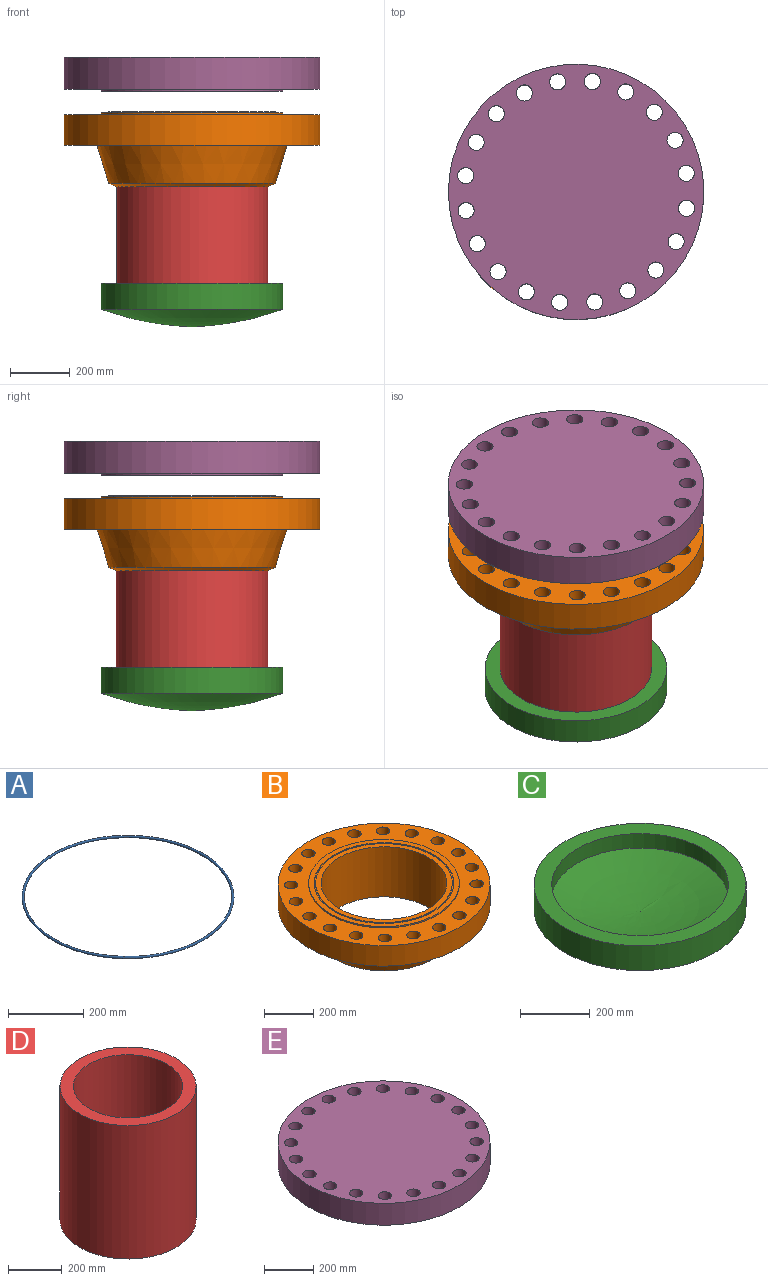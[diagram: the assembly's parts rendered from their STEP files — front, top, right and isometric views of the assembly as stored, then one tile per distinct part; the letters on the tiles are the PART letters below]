
ASSEMBLY  parts=5 mates=4
PART A: 1 faces, bbox 611.7x611.7x6.4 mm
  f0: torus R=279.4mm, axis (0,0,-1), area 35021.1mm2
PART B: 32 faces, bbox 857.3x857.3x247.7 mm
  f0: cylinder r=282.58mm len=565.15mm, axis (0,0,-1), area 7892mm2, adj f1,f11
  f1: plane 565.15x565.15mm, normal (0,0,1), area 11147.6mm2, adj f0,f2
  f2: cylinder r=276.23mm len=552.45mm, axis (0,0,-1), area 7714.6mm2, adj f1,f3
  f3: plane 552.45x552.45mm, normal (0,0,1), area 37021.3mm2, adj f2,f4
  f4: cylinder r=254mm len=508mm, axis (0,0,-1), area 395231.8mm2, adj f3,f5
  f5: cone r=254mm half-angle=67deg, axis (0,0,1), area 46560.4mm2, adj f4,f6
  f6: cone r=319.09mm half-angle=17deg, axis (0,0,1), area 253505.2mm2, adj f5,f7
  f7: plane 857.25x857.25mm, normal (0,0,-1), area 211322.6mm2, adj f6,f8,f12,f13,f14,f15,f16,f17
  f8: cylinder r=428.62mm len=857.25mm, axis (0,0,-1), area 273622mm2, adj f7,f9
  f9: plane 857.25x857.25mm, normal (0,0,1), area 239330.4mm2, adj f8,f10,f12,f13,f14,f15,f16,f17
  f10: cylinder r=304.8mm len=609.6mm, axis (0,0,-1), area 12161mm2, adj f9,f11
  f11: plane 609.6x609.6mm, normal (0,0,1), area 41011.6mm2, adj f0,f10
  f12: cylinder r=27.05mm len=101.6mm, axis (0,0,-1), area 17268.6mm2, adj f7,f9
  f13: cylinder r=27.05mm len=101.6mm, axis (0,0,-1), area 17268.6mm2, adj f7,f9
  f14: cylinder r=27.05mm len=101.6mm, axis (0,0,-1), area 17268.6mm2, adj f7,f9
  f15: cylinder r=27.05mm len=101.6mm, axis (0,0,-1), area 17268.6mm2, adj f7,f9
  f16: cylinder r=27.05mm len=101.6mm, axis (0,0,-1), area 17268.6mm2, adj f7,f9
  f17: cylinder r=27.05mm len=101.6mm, axis (0,0,-1), area 17268.6mm2, adj f7,f9
  f18: cylinder r=27.05mm len=101.6mm, axis (0,0,-1), area 17268.6mm2, adj f7,f9
  f19: cylinder r=27.05mm len=101.6mm, axis (0,0,-1), area 17268.6mm2, adj f7,f9
  f20: cylinder r=27.05mm len=101.6mm, axis (0,0,-1), area 17268.6mm2, adj f7,f9
  f21: cylinder r=27.05mm len=101.6mm, axis (0,0,-1), area 17268.6mm2, adj f7,f9
  f22: cylinder r=27.05mm len=101.6mm, axis (0,0,-1), area 17268.6mm2, adj f7,f9
  f23: cylinder r=27.05mm len=101.6mm, axis (0,0,-1), area 17268.6mm2, adj f7,f9
  f24: cylinder r=27.05mm len=101.6mm, axis (0,0,-1), area 17268.6mm2, adj f7,f9
  f25: cylinder r=27.05mm len=101.6mm, axis (0,0,-1), area 17268.6mm2, adj f7,f9
  f26: cylinder r=27.05mm len=101.6mm, axis (0,0,-1), area 17268.6mm2, adj f7,f9
  f27: cylinder r=27.05mm len=101.6mm, axis (0,0,-1), area 17268.6mm2, adj f7,f9
  f28: cylinder r=27.05mm len=101.6mm, axis (0,0,-1), area 17268.6mm2, adj f7,f9
  f29: cylinder r=27.05mm len=101.6mm, axis (0,0,-1), area 17268.6mm2, adj f7,f9
  f30: cylinder r=27.05mm len=101.6mm, axis (0,0,-1), area 17268.6mm2, adj f7,f9
  f31: cylinder r=27.05mm len=101.6mm, axis (0,0,-1), area 17268.6mm2, adj f7,f9
PART C: 5 faces, bbox 609.9x609.9x145.3 mm
  f0: revolved ~609.92x609.92mm, area 301686.6mm2, adj f1
  f1: cylinder r=304.96mm len=609.92mm, axis (0,0,1), area 166982mm2, adj f0,f2
  f2: plane 609.92x609.92mm, normal (0,0,1), area 89231mm2, adj f1,f3
  f3: cylinder r=254.16mm len=508.32mm, axis (0,0,1), area 81123.6mm2, adj f2,f4
  f4: revolved ~508.32x508.32mm, area 208213.8mm2, adj f3
PART D: 4 faces, bbox 508x508x609.6 mm
  f0: cylinder r=203.99mm len=609.6mm, axis (0,0,-1), area 781318.6mm2, adj f2,f3
  f1: cylinder r=254mm len=609.6mm, axis (0,0,-1), area 972878.4mm2, adj f2,f3
  f2: plane 508x508mm, normal (0,0,1), area 71958.6mm2, adj f0,f1
  f3: plane 508x508mm, normal (0,0,-1), area 71958.6mm2, adj f0,f1
PART E: 27 faces, bbox 857.3x857.3x115.3 mm
  f0: plane 609.6x609.6mm, normal (0,0,-1), area 41482mm2, adj f1,f6
  f1: cylinder r=304.8mm len=609.6mm, axis (0,0,-1), area 11698.7mm2, adj f0,f2
  f2: plane 857.25x857.25mm, normal (0,0,-1), area 239330.4mm2, adj f1,f3,f7,f8,f9,f10,f11,f12
  f3: cylinder r=428.62mm len=857.25mm, axis (0,0,-1), area 290723.4mm2, adj f2,f4
  f4: plane 857.25x857.25mm, normal (0,0,1), area 531193.9mm2, adj f3,f7,f8,f9,f10,f11,f12,f13
  f5: plane 552.98x552.98mm, normal (0,0,-1), area 240164.6mm2, adj f6
  f6: torus R=279.4mm, axis (0,0,-1), area 12923.1mm2, adj f0,f5
  f7: cylinder r=27.05mm len=107.95mm, axis (0,0,-1), area 18347.9mm2, adj f2,f4
  f8: cylinder r=27.05mm len=107.95mm, axis (0,0,-1), area 18347.9mm2, adj f2,f4
  f9: cylinder r=27.05mm len=107.95mm, axis (0,0,-1), area 18347.9mm2, adj f2,f4
  f10: cylinder r=27.05mm len=107.95mm, axis (0,0,-1), area 18347.9mm2, adj f2,f4
  f11: cylinder r=27.05mm len=107.95mm, axis (0,0,-1), area 18347.9mm2, adj f2,f4
  f12: cylinder r=27.05mm len=107.95mm, axis (0,0,-1), area 18347.9mm2, adj f2,f4
  f13: cylinder r=27.05mm len=107.95mm, axis (0,0,-1), area 18347.9mm2, adj f2,f4
  f14: cylinder r=27.05mm len=107.95mm, axis (0,0,-1), area 18347.9mm2, adj f2,f4
  f15: cylinder r=27.05mm len=107.95mm, axis (0,0,-1), area 18347.9mm2, adj f2,f4
  f16: cylinder r=27.05mm len=107.95mm, axis (0,0,-1), area 18347.9mm2, adj f2,f4
  f17: cylinder r=27.05mm len=107.95mm, axis (0,0,-1), area 18347.9mm2, adj f2,f4
  f18: cylinder r=27.05mm len=107.95mm, axis (0,0,-1), area 18347.9mm2, adj f2,f4
  f19: cylinder r=27.05mm len=107.95mm, axis (0,0,-1), area 18347.9mm2, adj f2,f4
  f20: cylinder r=27.05mm len=107.95mm, axis (0,0,-1), area 18347.9mm2, adj f2,f4
  f21: cylinder r=27.05mm len=107.95mm, axis (0,0,-1), area 18347.9mm2, adj f2,f4
  f22: cylinder r=27.05mm len=107.95mm, axis (0,0,-1), area 18347.9mm2, adj f2,f4
  f23: cylinder r=27.05mm len=107.95mm, axis (0,0,-1), area 18347.9mm2, adj f2,f4
  f24: cylinder r=27.05mm len=107.95mm, axis (0,0,-1), area 18347.9mm2, adj f2,f4
  f25: cylinder r=27.05mm len=107.95mm, axis (0,0,-1), area 18347.9mm2, adj f2,f4
  f26: cylinder r=27.05mm len=107.95mm, axis (0,0,-1), area 18347.9mm2, adj f2,f4
PLACE A t=(0,0,-173.99)mm
PLACE B t=(0,0,-175.26)mm
PLACE C t=(0,0,-188.84)mm
PLACE D t=(0,0,-181.61)mm
PLACE E t=(0,0,-102.63)mm
MATE fastened D.f0 <-> B.f0  axis (0,0,-1) through (0,0,427.99)mm
MATE fastened C.f1 <-> D.f0  axis (0,0,1) through (0,0,-181.61)mm
MATE slider E.f1 <-> D.f0  axis (0,0,1) through (0,0,621.03)mm
MATE fastened A.f0 <-> B.f0  axis (0,0,-1) through (0,0,434.34)mm
